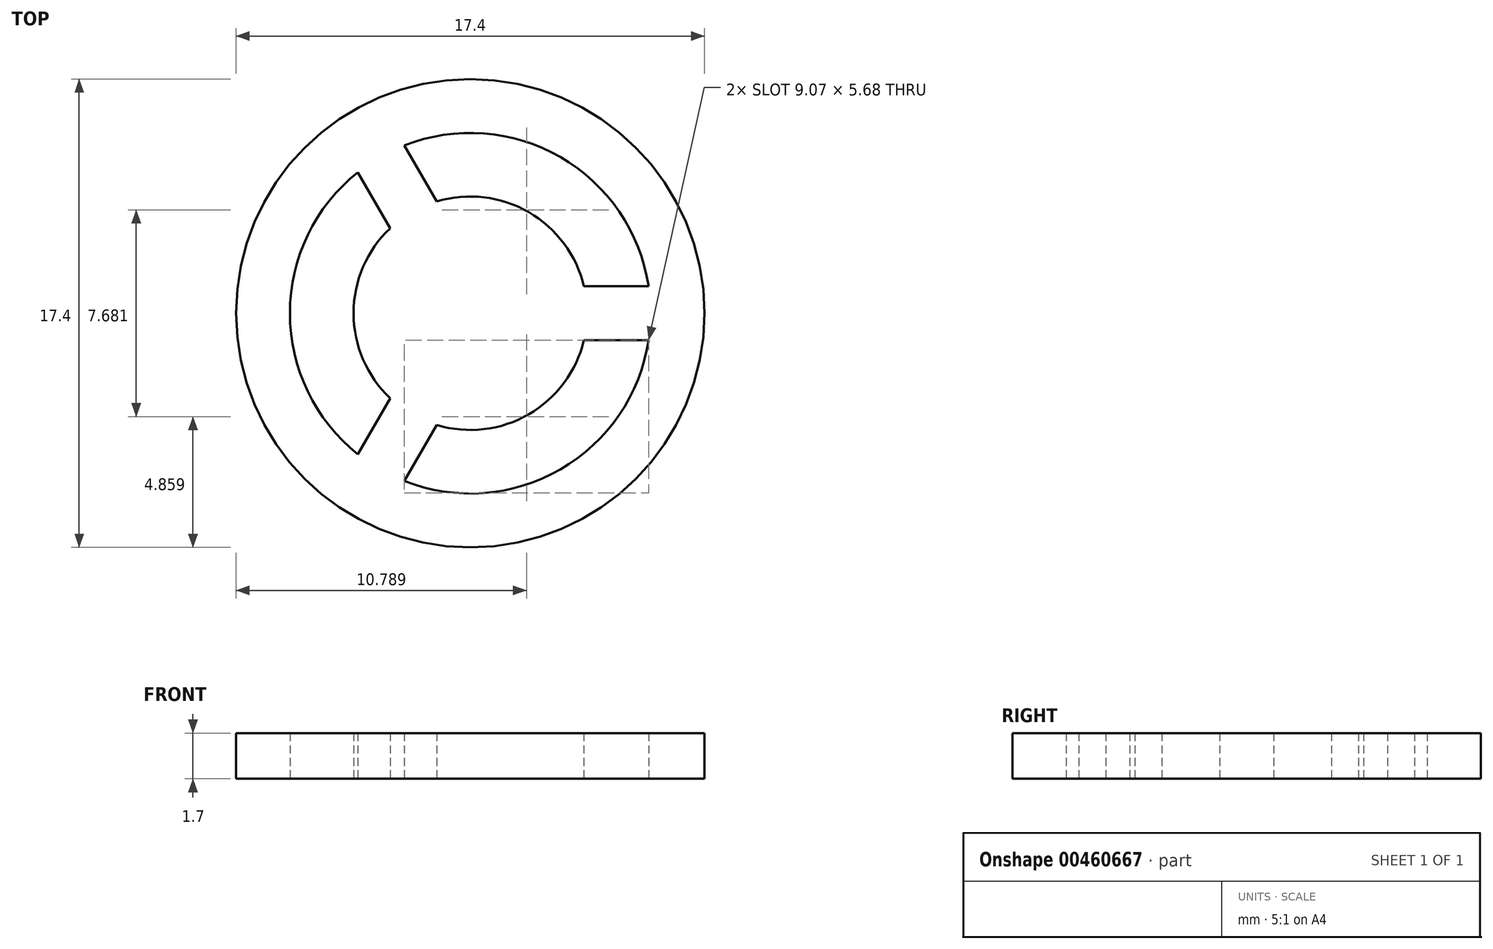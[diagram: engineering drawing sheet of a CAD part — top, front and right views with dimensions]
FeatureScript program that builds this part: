
annotation { "Feature Type Name" : "Feature", "Feature Type Description" : "" }
export const myFeature = defineFeature(function(context is Context, id is Id, definition is map)
    precondition{}
    {
        {
            var Q0;
            Q0=qCreatedBy(makeId("Top.planeOp"),FACE);
            var sketch = newSketch(context, id + "F0", { "sketchPlane" : qUnion([Q0]), "disableImprinting" : false});
            skCircle(sketch, "E0", {"center": v(0, 0) * mm, "radius": 8.7 * mm});
            skArc(sketch, "E1", {"start": v(-2.98, 3.16) * mm, "mid": v(-4.34, 0) * mm, "end": v(-2.98, -3.16) * mm});
            skArc(sketch, "E2.0", {"start": v(-4.18, 5.24) * mm, "mid": v(-6.7, 0) * mm, "end": v(-4.18, -5.24) * mm});
            skLineSegment(sketch, "E3.0", {"start": v(4.22, 1) * mm, "end": v(6.62, 1) * mm});
            skLineSegment(sketch, "E4.0", {"start": v(4.22, -1) * mm, "end": v(6.62, -1) * mm});
            skLineSegment(sketch, "E5.1.0", {"start": v(-1.24, 4.16) * mm, "end": v(-2.45, 6.24) * mm});
            skLineSegment(sketch, "E5.1.1", {"start": v(-2.98, 3.16) * mm, "end": v(-4.18, 5.24) * mm});
            skLineSegment(sketch, "E5.2.0", {"start": v(-2.98, -3.16) * mm, "end": v(-4.18, -5.24) * mm});
            skLineSegment(sketch, "E5.2.1", {"start": v(-1.24, -4.16) * mm, "end": v(-2.45, -6.24) * mm});
            skArc(sketch, "E6.trimOffspring", {"start": v(6.62, 1) * mm, "mid": v(3.35, 5.8) * mm, "end": v(-2.45, 6.24) * mm});
            skArc(sketch, "E7.trimOffspring", {"start": v(-1.24, -4.16) * mm, "mid": v(2.17, -3.76) * mm, "end": v(4.22, -1) * mm});
            skArc(sketch, "E8.trimOffspring", {"start": v(-2.45, -6.24) * mm, "mid": v(3.35, -5.8) * mm, "end": v(6.62, -1) * mm});
            skArc(sketch, "E9.trimOffspring", {"start": v(4.22, 1) * mm, "mid": v(2.17, 3.76) * mm, "end": v(-1.24, 4.16) * mm});
            skSolve(sketch);
        }
        {
            var Q0;
            Q0=makeQuery(id+"F0.imprint","IMPRINT",FACE,{"disambiguationData":[TD([[makeQuery(id+"F0.imprint","IMPRINT",EDGE,{"derivedFrom":sQuery(id+"F0.wireOp",EDGE,"E0")}),1.0]])]});
            extrude(context, id + "F1", {"entities" : qUnion([Q0]), "depth" : 1.7 * mm});
        }
    });
